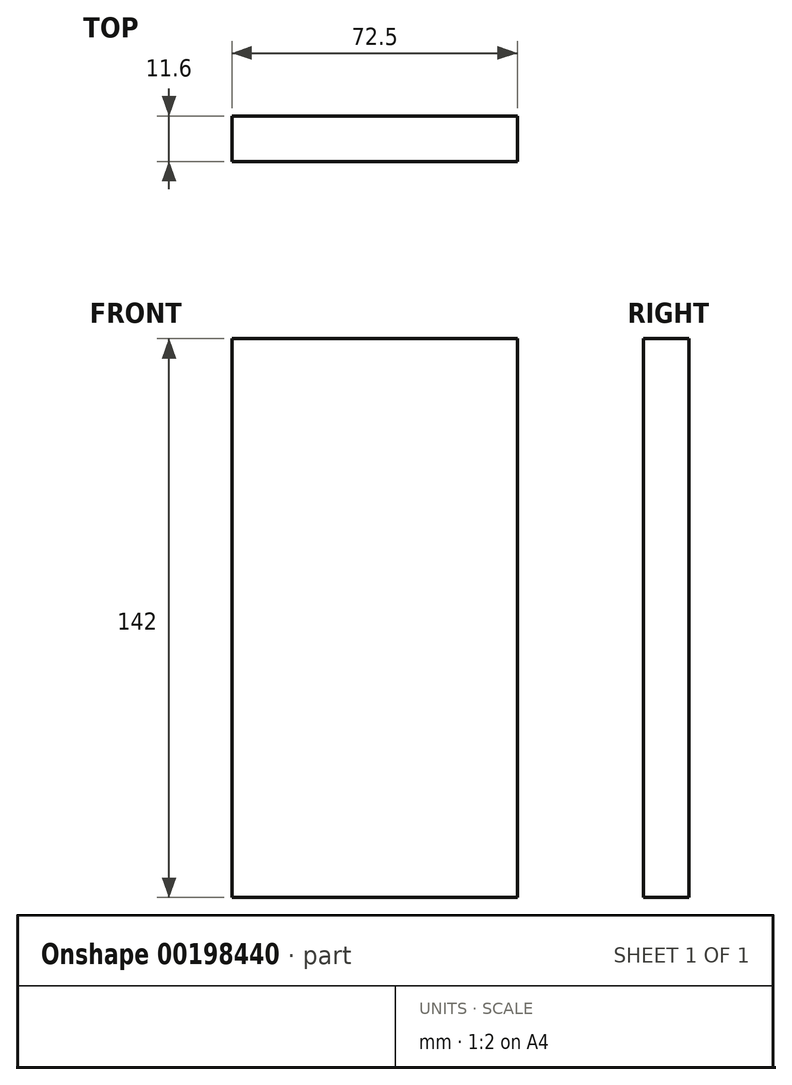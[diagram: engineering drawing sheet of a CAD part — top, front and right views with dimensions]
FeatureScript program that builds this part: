
annotation { "Feature Type Name" : "Feature", "Feature Type Description" : "" }
export const myFeature = defineFeature(function(context is Context, id is Id, definition is map)
    precondition{}
    {
        {
            var Q0;
            Q0=qCreatedBy(makeId("Front.planeOp"),FACE);
            var sketch = newSketch(context, id + "F0", { "sketchPlane" : qUnion([Q0])});
            skLineSegment(sketch, "E0.bottom", {"start": v(36.25, 71) * mm, "end": v(-36.25, 71) * mm});
            skLineSegment(sketch, "E0.top", {"start": v(36.25, -71) * mm, "end": v(-36.25, -71) * mm});
            skLineSegment(sketch, "E0.left", {"start": v(36.25, 71) * mm, "end": v(36.25, -71) * mm});
            skLineSegment(sketch, "E0.right", {"start": v(-36.25, 71) * mm, "end": v(-36.25, -71) * mm});
            skPoint(sketch, "E0.middle", {"position": v(0, 0) * mm});
            skSolve(sketch);
        }
        {
            var Q0;
            Q0=makeQuery(id+"F0.imprint","IMPRINT",FACE,{"disambiguationData":[TD([[makeQuery(id+"F0.imprint","IMPRINT",EDGE,{"derivedFrom":sQuery(id+"F0.wireOp",EDGE,"E0.bottom")}),1.0]])]});
            extrude(context, id + "F1", {"entities" : qUnion([Q0]), "oppositeDirection" : true, "depth" : 11.6 * mm});
        }
    });
